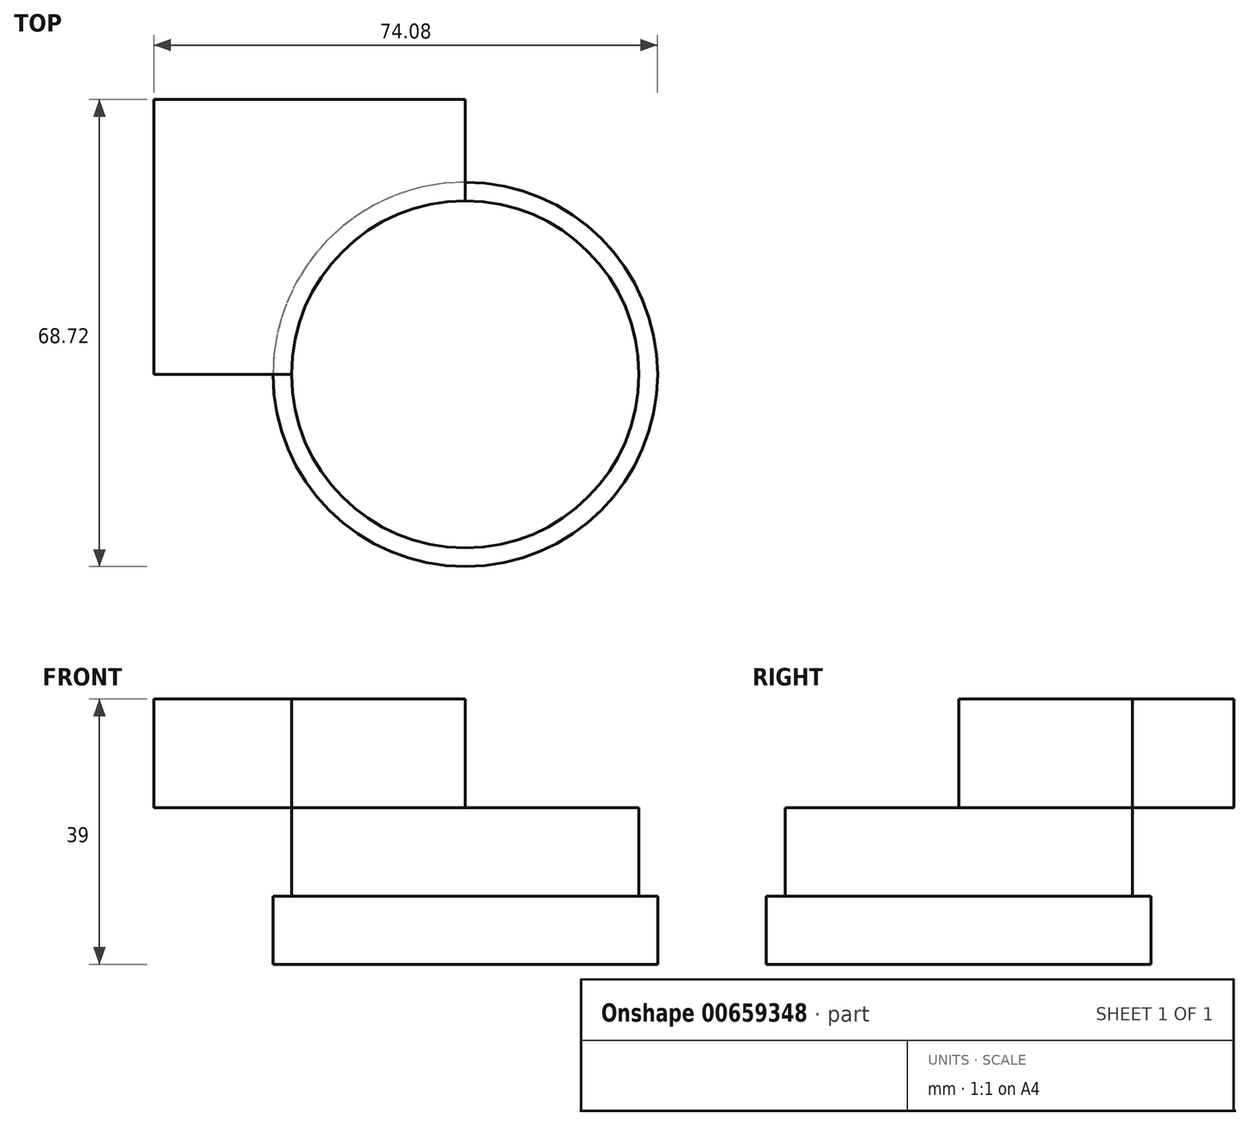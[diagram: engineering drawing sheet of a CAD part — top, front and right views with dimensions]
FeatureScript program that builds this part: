
annotation { "Feature Type Name" : "Feature", "Feature Type Description" : "" }
export const myFeature = defineFeature(function(context is Context, id is Id, definition is map)
    precondition{}
    {
        {
            var Q0;
            Q0=qCreatedBy(makeId("Top.planeOp"),FACE);
            var sketch = newSketch(context, id + "F0", { "sketchPlane" : qUnion([Q0])});
            skCircle(sketch, "E0", {"center": v(0, 0) * mm, "radius": 28.28 * mm});
            skSolve(sketch);
        }
        {
            var Q0;
            Q0=makeQuery(id+"F0.imprint","IMPRINT",FACE,{"disambiguationData":[TD([[makeQuery(id+"F0.imprint","IMPRINT",EDGE,{"derivedFrom":sQuery(id+"F0.wireOp",EDGE,"E0")}),1.0]])]});
            extrude(context, id + "F1", {"entities" : qUnion([Q0]), "depth" : 10 * mm, "offsetDistance" : 25.4 * mm});
        }
        {
            var Q0;
            Q0=makeQuery(id+"F1.opExtrude","CAP_FACE",FACE,{"disambiguationData":[OSD([sQuery(id+"F0.wireOp",EDGE,"E0")])],"isStart":false});
            var sketch = newSketch(context, id + "F2", { "sketchPlane" : qUnion([Q0])});
            skCircle(sketch, "E1", {"center": v(0, 0) * mm, "radius": 25.54 * mm});
            skSolve(sketch);
        }
        {
            var Q0;
            Q0=makeQuery(id+"F2.imprint","IMPRINT",FACE,{"disambiguationData":[TD([[makeQuery(id+"F2.imprint","IMPRINT",EDGE,{"derivedFrom":sQuery(id+"F2.wireOp",EDGE,"E1")}),1.0]])]});
            extrude(context, id + "F3", {"entities" : qUnion([Q0]), "operationType" : NewBodyOperationType.ADD, "depth" : 13 * mm, "offsetDistance" : 25.4 * mm});
        }
        {
            var Q0;
            Q0=makeQuery(id+"F3.opExtrude","CAP_FACE",FACE,{"disambiguationData":[OSD([sQuery(id+"F2.wireOp",EDGE,"E1")])],"isStart":false});
            var sketch = newSketch(context, id + "F4", { "sketchPlane" : qUnion([Q0])});
            skSolve(sketch);
        }
        {
            var Q0;
            Q0=makeQuery(id+"F4.imprint","IMPRINT",FACE,{"disambiguationData":[TD([[makeQuery(id+"F4.imprint","IMPRINT",EDGE,{"derivedFrom":makeQuery(id+"F3.opExtrude","CAP_EDGE",EDGE,{"disambiguationData":[OSD([sQuery(id+"F2.wireOp",EDGE,"E1")])],"isStart":false})}),1.0]])]});
            var sketch = newSketch(context, id + "F5", { "sketchPlane" : qUnion([Q0])});
            skLineSegment(sketch, "E2.bottom", {"start": v(0, 0) * mm, "end": v(-45.8, 0) * mm});
            skLineSegment(sketch, "E2.top", {"start": v(0, 40.44) * mm, "end": v(-45.8, 40.44) * mm});
            skLineSegment(sketch, "E2.left", {"start": v(0, 0) * mm, "end": v(0, 40.44) * mm});
            skLineSegment(sketch, "E2.right", {"start": v(-45.8, 0) * mm, "end": v(-45.8, 40.44) * mm});
            skSolve(sketch);
        }
        {
            var Q0;
            {var subQ2=sQuery(id+"F5.wireOp",EDGE,"E2.top");Q0=makeQuery(id+"F5.imprint","IMPRINT",FACE,{"disambiguationData":[TD([[makeQuery(id+"F5.imprint","IMPRINT",EDGE,{"derivedFrom":subQ2}),1.0]])]});}
            extrude(context, id + "F6", {"entities" : qUnion([Q0]), "operationType" : NewBodyOperationType.ADD, "depth" : 16 * mm, "offsetDistance" : 25.4 * mm});
        }
    });
